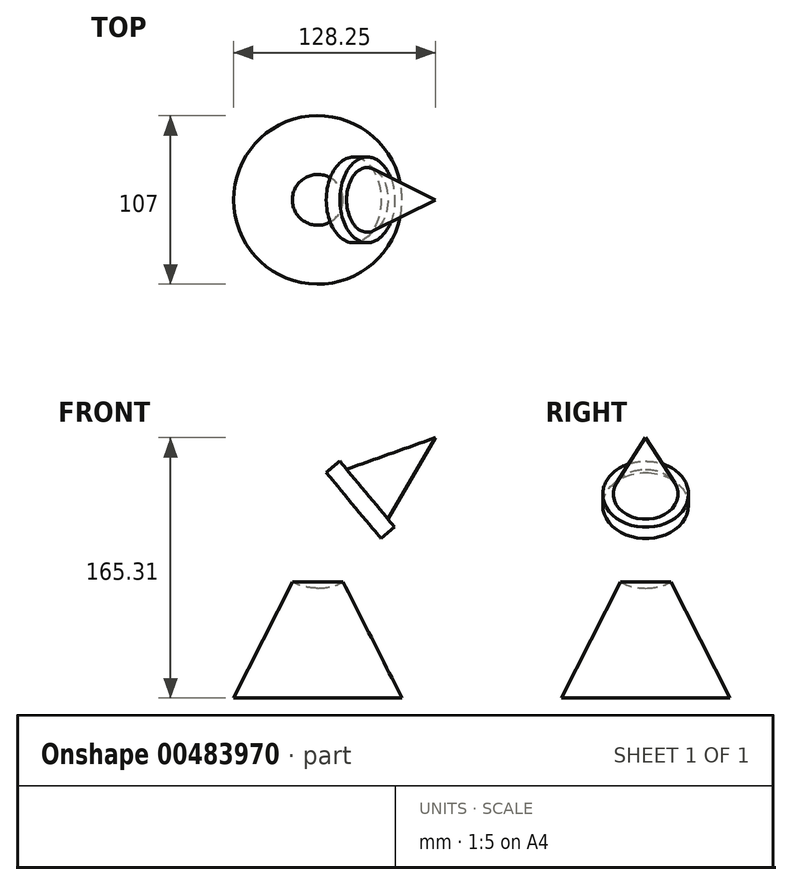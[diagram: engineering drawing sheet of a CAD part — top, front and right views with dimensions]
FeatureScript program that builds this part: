
annotation { "Feature Type Name" : "Feature", "Feature Type Description" : "" }
export const myFeature = defineFeature(function(context is Context, id is Id, definition is map)
    precondition{}
    {
        {
            var Q0;
            Q0=qCreatedBy(makeId("Front.planeOp"),FACE);
            var sketch = newSketch(context, id + "F0", { "sketchPlane" : qUnion([Q0])});
            skLineSegment(sketch, "E0", {"start": v(0, 27.64) * mm, "end": v(-53.5, -77.57) * mm});
            skLineSegment(sketch, "E1", {"start": v(-53.5, -77.57) * mm, "end": v(0, -77.57) * mm});
            skLineSegment(sketch, "E2", {"start": v(0, -77.57) * mm, "end": v(0, 27.64) * mm});
            skCircle(sketch, "E3", {"center": v(0, 27.64) * mm, "radius": 35.56 * mm});
            skLineSegment(sketch, "E4", {"start": v(0, 27.64) * mm, "end": v(0, 63.2) * mm});
            skLineSegment(sketch, "E5", {"start": v(0, 63.2) * mm, "end": v(0, -7.92) * mm});
            skSolve(sketch);
        }
        {
            var Q0;
            Q0=qCreatedBy(makeId("Front.planeOp"),FACE);
            var sketch = newSketch(context, id + "F1", { "sketchPlane" : qUnion([Q0])});
            skLineSegment(sketch, "E6", {"start": v(5.35, 65.54) * mm, "end": v(22.74, 44.58) * mm});
            skLineSegment(sketch, "E7", {"start": v(5.35, 65.54) * mm, "end": v(14.04, 72.75) * mm});
            skPoint(sketch, "E7.endSnap0", {"position": v(14.04, 55.06) * mm});
            skLineSegment(sketch, "E8", {"start": v(14.04, 72.75) * mm, "end": v(30.4, 53.04) * mm});
            skLineSegment(sketch, "E9", {"start": v(22.74, 44.58) * mm, "end": v(74.75, 87.74) * mm});
            skLineSegment(sketch, "E10", {"start": v(74.75, 87.74) * mm, "end": v(18.29, 67.63) * mm});
            skSolve(sketch);
        }
        {
            var Q0;
            {var subQ0=sQuery(id+"F0.wireOp",EDGE,"E5");var subQ1=sQuery(id+"F0.wireOp",EDGE,"E0");var subQ2=makeQuery(id+"F0.imprint","INTERSECT",VERTEX,{"derivedFrom":[subQ1,subQ0]});Q0=makeQuery(id+"F0.imprint","IMPRINT",FACE,{"disambiguationData":[TD([[makeQuery(id+"F0.imprint","IMPRINT",EDGE,{"disambiguationData":[TD([[subQ2,-1.0]])],"derivedFrom":subQ1}),-1.0]])]});}
            var Q1;
            {var subQ0=sQuery(id+"F0.wireOp",EDGE,"E5");var subQ1=sQuery(id+"F0.wireOp",EDGE,"E0");var subQ2=makeQuery(id+"F0.imprint","INTERSECT",VERTEX,{"derivedFrom":[subQ1,subQ0]});Q1=makeQuery(id+"F0.imprint","IMPRINT",FACE,{"disambiguationData":[TD([[makeQuery(id+"F0.imprint","IMPRINT",EDGE,{"disambiguationData":[TD([[subQ2,-1.0]])],"derivedFrom":subQ1}),1.0]])]});}
            var Q2;
            {var subQ0=sQuery(id+"F0.wireOp",EDGE,"E1");Q2=makeQuery(id+"F0.imprint","IMPRINT",FACE,{"disambiguationData":[TD([[makeQuery(id+"F0.imprint","IMPRINT",EDGE,{"derivedFrom":subQ0}),1.0]])]});}
            var Q3;
            Q3=sQuery(id+"F0.wireOp",EDGE,"E5");
            revolve(context, id + "F2", {"entities" : qUnion([Q0, Q1, Q2]), "axis" : qUnion([Q3]), "revolveType" : RevolveType.FULL});
        }
        {
            var Q0;
            Q0=makeQuery(id+"F1.imprint","IMPRINT",FACE,{"disambiguationData":[TD([[makeQuery(id+"F1.imprint","IMPRINT",EDGE,{"derivedFrom":sQuery(id+"F1.wireOp",EDGE,"E6")}),1.0]])]});
            var Q1;
            Q1=sQuery(id+"F1.wireOp",EDGE,"E9");
            revolve(context, id + "F3", {"operationType" : NewBodyOperationType.ADD, "entities" : qUnion([Q0]), "axis" : qUnion([Q1]), "revolveType" : RevolveType.FULL});
        }
    });
